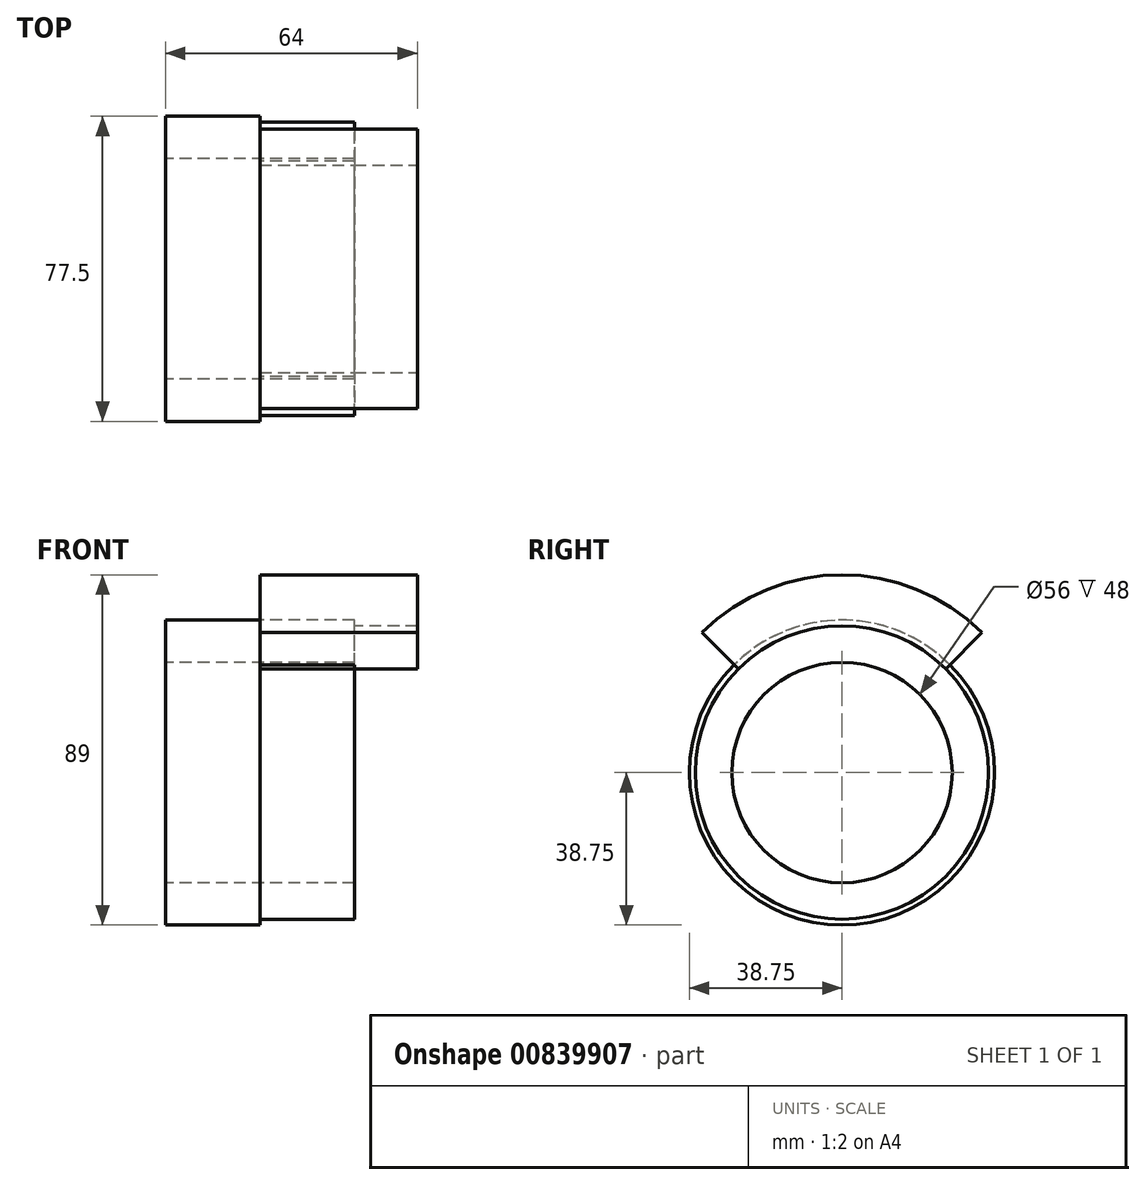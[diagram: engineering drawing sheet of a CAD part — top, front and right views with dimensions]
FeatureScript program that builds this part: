
annotation { "Feature Type Name" : "Feature", "Feature Type Description" : "" }
export const myFeature = defineFeature(function(context is Context, id is Id, definition is map)
    precondition{}
    {
        {
            var Q0;
            Q0=qCreatedBy(makeId("Right.planeOp"),FACE);
            var sketch = newSketch(context, id + "F0", { "sketchPlane" : qUnion([Q0])});
            skCircle(sketch, "E0", {"center": v(0, 0) * mm, "radius": 38.75 * mm});
            skCircle(sketch, "E1", {"center": v(0, 0) * mm, "radius": 28 * mm});
            skSolve(sketch);
        }
        {
            var Q0;
            Q0=makeQuery(id+"F0.imprint","IMPRINT",FACE,{"disambiguationData":[TD([[makeQuery(id+"F0.imprint","IMPRINT",EDGE,{"derivedFrom":sQuery(id+"F0.wireOp",EDGE,"E0")}),1.0]])]});
            extrude(context, id + "F1", {"entities" : qUnion([Q0]), "depth" : 48 * mm, "offsetDistance" : 25 * mm});
        }
        {
            var Q0;
            Q0=qCreatedBy(makeId("Front.planeOp"),FACE);
            var sketch = newSketch(context, id + "F2", { "sketchPlane" : qUnion([Q0])});
            skLineSegment(sketch, "E2", {"start": v(0, 0) * mm, "end": v(0, 38.75) * mm});
            skLineSegment(sketch, "E3", {"start": v(24, 38.75) * mm, "end": v(24, 50.25) * mm});
            skLineSegment(sketch, "E4", {"start": v(24, 50.25) * mm, "end": v(64, 50.25) * mm});
            skLineSegment(sketch, "E5", {"start": v(64, 50.25) * mm, "end": v(64, 37.25) * mm});
            skLineSegment(sketch, "E6", {"start": v(64, 37.25) * mm, "end": v(48, 37.25) * mm});
            skLineSegment(sketch, "E7", {"start": v(48, 37.25) * mm, "end": v(48, 38.75) * mm});
            skLineSegment(sketch, "E8", {"start": v(48, 38.75) * mm, "end": v(24, 38.75) * mm});
            skSolve(sketch);
        }
        {
            var Q0;
            Q0=makeQuery(id+"F2.imprint","IMPRINT",FACE,{"disambiguationData":[TD([[makeQuery(id+"F2.imprint","IMPRINT",EDGE,{"derivedFrom":sQuery(id+"F2.wireOp",EDGE,"E3")}),-1.0]])]});
            var Q1;
            Q1=makeQuery(id+"F1.opExtrude","CAP_EDGE",EDGE,{"disambiguationData":[OSD([sQuery(id+"F0.wireOp",EDGE,"E1")])],"isStart":false});
            revolve(context, id + "F3", {"surfaceOperationType" : NewSurfaceOperationType.NEW, "entities" : qUnion([Q0]), "axis" : qUnion([Q1]), "revolveType" : RevolveType.FULL});
        }
        {
            var Q0;
            Q0=makeQuery(id+"F3.opRevolve","SWEPT_FACE",FACE,{"disambiguationData":[OSD([sQuery(id+"F2.wireOp",EDGE,"E5")])]});
            var sketch = newSketch(context, id + "F4", { "sketchPlane" : qUnion([Q0])});
            skLineSegment(sketch, "E9", {"start": v(-26.34, 26.34) * mm, "end": v(-35.53, 35.53) * mm});
            skLineSegment(sketch, "E10.MirrorCS", {"start": v(26.34, 26.34) * mm, "end": v(35.53, 35.53) * mm});
            skArc(sketch, "E11", {"start": v(-35.53, 35.53) * mm, "mid": v(0, -50.25) * mm, "end": v(35.53, 35.53) * mm});
            skSolve(sketch);
        }
        {
            var Q0;
            {var subQ0=sQuery(id+"F4.wireOp",EDGE,"E9");Q0=makeQuery(id+"F4.imprint","IMPRINT",FACE,{"disambiguationData":[TD([[makeQuery(id+"F4.imprint","IMPRINT",EDGE,{"derivedFrom":subQ0}),1.0]])]});}
            extrude(context, id + "F5", {"entities" : qUnion([Q0]), "operationType" : NewBodyOperationType.REMOVE, "oppositeDirection" : true, "depth" : 40 * mm, "offsetDistance" : 25 * mm});
        }
    });
